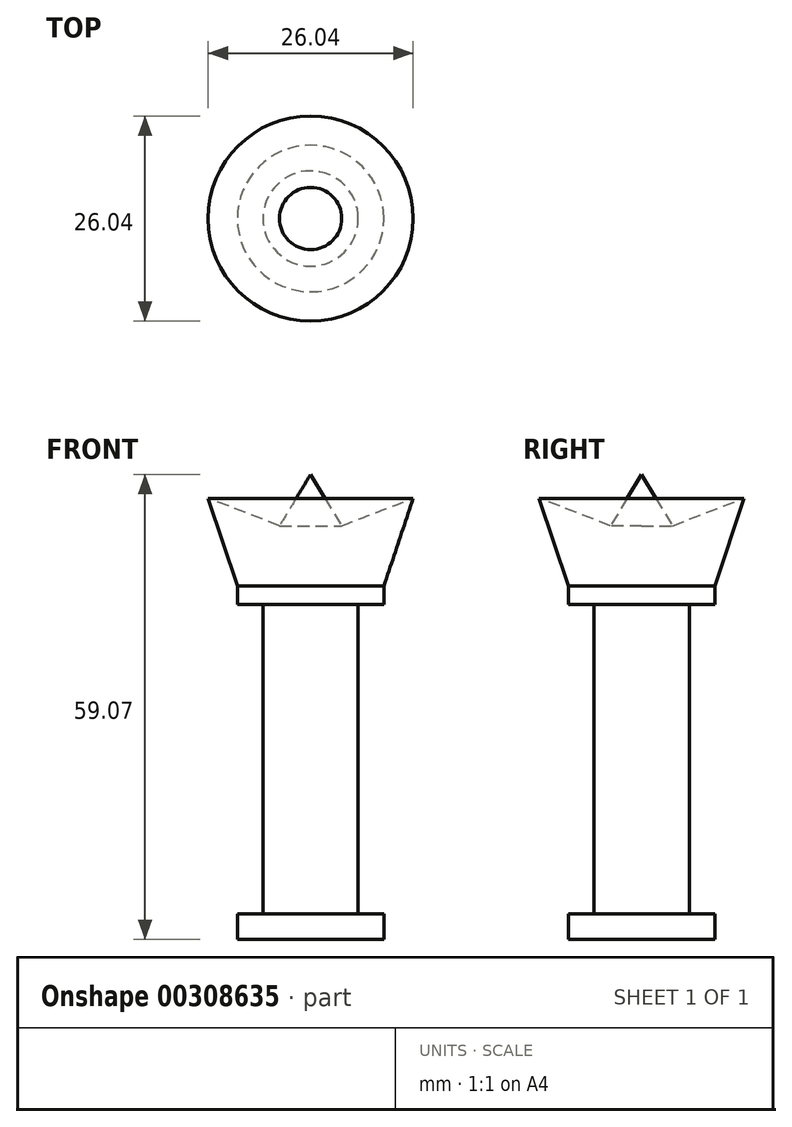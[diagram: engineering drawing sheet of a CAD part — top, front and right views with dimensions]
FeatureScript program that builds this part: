
annotation { "Feature Type Name" : "Feature", "Feature Type Description" : "" }
export const myFeature = defineFeature(function(context is Context, id is Id, definition is map)
    precondition{}
    {
        {
            var Q0;
            Q0=qCreatedBy(makeId("Front.planeOp"),FACE);
            var sketch = newSketch(context, id + "F0", { "sketchPlane" : qUnion([Q0])});
            skLineSegment(sketch, "E0", {"start": v(0, 29.07) * mm, "end": v(0, -30) * mm});
            skLineSegment(sketch, "E1", {"start": v(0, -30) * mm, "end": v(-9.3, -30) * mm});
            skLineSegment(sketch, "E2", {"start": v(-9.3, -30) * mm, "end": v(-9.3, -26.75) * mm});
            skLineSegment(sketch, "E3", {"start": v(-9.3, -26.75) * mm, "end": v(-6.05, -26.75) * mm});
            skLineSegment(sketch, "E4", {"start": v(-6.05, -26.75) * mm, "end": v(-6.05, 12.56) * mm});
            skLineSegment(sketch, "E5", {"start": v(-6.05, 12.56) * mm, "end": v(-9.3, 12.56) * mm});
            skLineSegment(sketch, "E6", {"start": v(-9.3, 12.56) * mm, "end": v(-9.3, 14.89) * mm});
            skLineSegment(sketch, "E7", {"start": v(-9.3, 14.89) * mm, "end": v(-13.02, 26.05) * mm});
            skLineSegment(sketch, "E8", {"start": v(-13.02, 26.05) * mm, "end": v(-3.95, 22.56) * mm});
            skLineSegment(sketch, "E9", {"start": v(-3.95, 22.56) * mm, "end": v(0, 29.07) * mm});
            skSolve(sketch);
        }
        {
            var Q0;
            Q0 = qSketchRegion(id + "F0", true);
            var Q1;
            Q1=sQuery(id+"F0.wireOp",EDGE,"E0");
            revolve(context, id + "F1", {"entities" : qUnion([Q0]), "axis" : qUnion([Q1]), "revolveType" : RevolveType.FULL});
        }
    });
